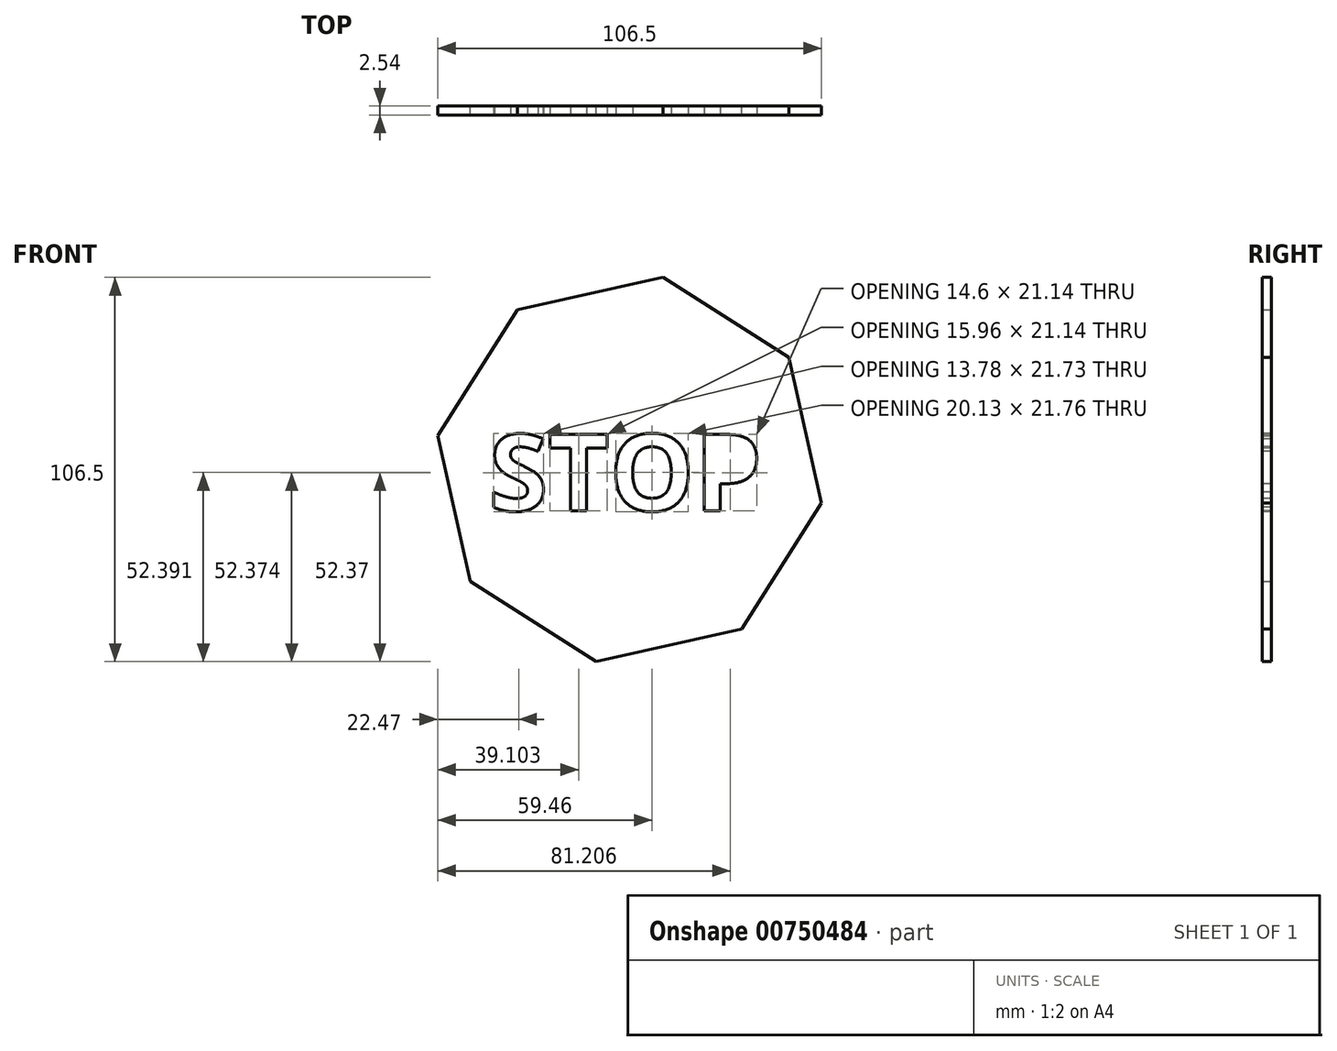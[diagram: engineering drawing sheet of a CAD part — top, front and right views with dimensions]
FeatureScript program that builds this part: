
annotation { "Feature Type Name" : "Feature", "Feature Type Description" : "" }
export const myFeature = defineFeature(function(context is Context, id is Id, definition is map)
    precondition{}
    {
        {
            var Q0;
            Q0=qCreatedBy(makeId("Front.planeOp"),FACE);
            var sketch = newSketch(context, id + "F0", { "sketchPlane" : qUnion([Q0])});
            skLineSegment(sketch, "E0.0", {"start": v(53.25, -9.32) * mm, "end": v(31.06, -44.25) * mm});
            skLineSegment(sketch, "E0.1", {"start": v(31.06, -44.25) * mm, "end": v(-9.32, -53.25) * mm});
            skLineSegment(sketch, "E0.2", {"start": v(-9.32, -53.25) * mm, "end": v(-44.25, -31.06) * mm});
            skLineSegment(sketch, "E0.3", {"start": v(-44.25, -31.06) * mm, "end": v(-53.25, 9.32) * mm});
            skLineSegment(sketch, "E0.4", {"start": v(-53.25, 9.32) * mm, "end": v(-31.06, 44.25) * mm});
            skLineSegment(sketch, "E0.5", {"start": v(-31.06, 44.25) * mm, "end": v(9.32, 53.25) * mm});
            skLineSegment(sketch, "E0.6", {"start": v(9.32, 53.25) * mm, "end": v(44.25, 31.06) * mm});
            skLineSegment(sketch, "E0.7", {"start": v(44.25, 31.06) * mm, "end": v(53.25, -9.32) * mm});
            skPoint(sketch, "E0.0.midPoint", {"position": v(42.16, -26.79) * mm});
            skPoint(sketch, "E1.0.midPoint", {"position": v(42.02, -21.88) * mm});
            skPoint(sketch, "E2.0.midPoint", {"position": v(27.79, -29.94) * mm});
            skPoint(sketch, "E3.orphan", {"position": v(26.24, 34.65) * mm});
            skPoint(sketch, "E4.orphan", {"position": v(-2.18, 43.41) * mm});
            skPoint(sketch, "E5.orphan", {"position": v(16.9, -40.05) * mm});
            skPoint(sketch, "E6.orphan", {"position": v(38.68, -19.82) * mm});
            skPoint(sketch, "E1.0.start.orphan", {"position": v(51.08, -4.48) * mm});
            skPoint(sketch, "E7.trimOffspring.end.orphan", {"position": v(32.95, -39.29) * mm});
            skLineSegment(sketch, "E8.trimOffspring", {"start": v(-49.94, 0.86) * mm, "end": v(-51.08, 4.48) * mm});
            skArc(sketch, "E9.trimOffspring", {"start": v(-0.86, -49.94) * mm, "mid": v(5.04, -49.7) * mm, "end": v(10.87, -48.75) * mm, "construction": true});
            skArc(sketch, "E10.trimOffspring", {"start": v(-49.94, 0.86) * mm, "mid": v(-49.7, -5.04) * mm, "end": v(-48.75, -10.87) * mm, "construction": true});
            skArc(sketch, "E11.trimOffspring", {"start": v(-34.7, 35.92) * mm, "mid": v(-38.7, 31.57) * mm, "end": v(-42.16, 26.79) * mm, "construction": true});
            skSolve(sketch);
        }
        {
            var Q0;
            Q0=makeQuery(id+"F0.imprint","IMPRINT",FACE,{"disambiguationData":[TD([[makeQuery(id+"F0.imprint","IMPRINT",EDGE,{"derivedFrom":sQuery(id+"F0.wireOp",EDGE,"E0.0")}),-1.0]])]});
            var Q1;
            Q1=makeQuery(id+"F0.imprint","IMPRINT",FACE,{"disambiguationData":[TD([[makeQuery(id+"F0.imprint","IMPRINT",EDGE,{"derivedFrom":sQuery(id+"F0.wireOp",EDGE,"E2.0")}),-1.0]])]});
            var Q2;
            Q2=makeQuery(id+"F0.imprint","IMPRINT",FACE,{"disambiguationData":[TD([[makeQuery(id+"F0.imprint","IMPRINT",EDGE,{"derivedFrom":sQuery(id+"F0.wireOp",EDGE,"E1.0")}),-1.0]])]});
            extrude(context, id + "F1", {"entities" : qUnion([Q0, Q1, Q2]), "depth" : 2.54 * mm, "offsetDistance" : 25.4 * mm});
        }
        {
            var Q0;
            Q0=qCreatedBy(makeId("Front.planeOp"),FACE);
            var sketch = newSketch(context, id + "F2", { "sketchPlane" : qUnion([Q0])});
            skPoint(sketch, "E12.0.midPoint", {"position": v(25, -5.92) * mm});
            skPoint(sketch, "E13.orphan", {"position": v(14.87, 21.73) * mm});
            skPoint(sketch, "E12.7.end.orphan", {"position": v(26.88, 4.44) * mm});
            skPoint(sketch, "E14.orphan", {"position": v(23.13, -16.28) * mm});
            skPoint(sketch, "E15.orphan", {"position": v(5.84, -28.28) * mm});
            skPoint(sketch, "E16.orphan", {"position": v(-14.87, -24.54) * mm});
            skPoint(sketch, "E17.orphan", {"position": v(-26.88, -7.25) * mm});
            skPoint(sketch, "E18.orphan", {"position": v(-23.13, 13.47) * mm});
            skText(sketch, "E19", { "text": "STOP", "fontName": "OpenSans-Bold.ttf"});
            const initialGuessF2  = {"E19": [-0.03903, -0.01145, 1, 0, 0.02132]};
            skSetInitialGuess(sketch, initialGuessF2);
            skSolve(sketch);
        }
        {
            var Q0;
            Q0 = qSketchRegion(id + "F2", true);
            extrude(context, id + "F3", {"entities" : qUnion([Q0]), "operationType" : NewBodyOperationType.ADD, "depth" : 2.8 * mm, "offsetDistance" : 25.4 * mm});
        }
        {
            var Q0;
            Q0=makeQuery(id+"F3.opExtrude","CAP_FACE",FACE,{"disambiguationData":[OSD([sQuery(id+"F2.wireOp",EDGE,"E19.sketch_text.stroke-28"),sQuery(id+"F2.wireOp",EDGE,"E19.sketch_text.stroke-29"),sQuery(id+"F2.wireOp",EDGE,"E19.sketch_text.stroke-30"),sQuery(id+"F2.wireOp",EDGE,"E19.sketch_text.stroke-31"),sQuery(id+"F2.wireOp",EDGE,"E19.sketch_text.stroke-32"),sQuery(id+"F2.wireOp",EDGE,"E19.sketch_text.stroke-33"),sQuery(id+"F2.wireOp",EDGE,"E19.sketch_text.stroke-34"),sQuery(id+"F2.wireOp",EDGE,"E19.sketch_text.stroke-35")])],"isStart":false});
            extrude(context, id + "F4", {"entities" : qUnion([Q0]), "operationType" : NewBodyOperationType.REMOVE, "oppositeDirection" : true, "depth" : 25.4 * mm, "offsetDistance" : 25.4 * mm});
        }
        {
            var Q0;
            Q0=makeQuery(id+"F3.opExtrude","CAP_FACE",FACE,{"disambiguationData":[OSD([sQuery(id+"F2.wireOp",EDGE,"E19.sketch_text.stroke-0"),sQuery(id+"F2.wireOp",EDGE,"E19.sketch_text.stroke-1"),sQuery(id+"F2.wireOp",EDGE,"E19.sketch_text.stroke-2"),sQuery(id+"F2.wireOp",EDGE,"E19.sketch_text.stroke-3"),sQuery(id+"F2.wireOp",EDGE,"E19.sketch_text.stroke-4"),sQuery(id+"F2.wireOp",EDGE,"E19.sketch_text.stroke-5"),sQuery(id+"F2.wireOp",EDGE,"E19.sketch_text.stroke-6"),sQuery(id+"F2.wireOp",EDGE,"E19.sketch_text.stroke-7"),sQuery(id+"F2.wireOp",EDGE,"E19.sketch_text.stroke-8"),sQuery(id+"F2.wireOp",EDGE,"E19.sketch_text.stroke-9"),sQuery(id+"F2.wireOp",EDGE,"E19.sketch_text.stroke-10"),sQuery(id+"F2.wireOp",EDGE,"E19.sketch_text.stroke-11"),sQuery(id+"F2.wireOp",EDGE,"E19.sketch_text.stroke-12"),sQuery(id+"F2.wireOp",EDGE,"E19.sketch_text.stroke-13"),sQuery(id+"F2.wireOp",EDGE,"E19.sketch_text.stroke-14"),sQuery(id+"F2.wireOp",EDGE,"E19.sketch_text.stroke-15"),sQuery(id+"F2.wireOp",EDGE,"E19.sketch_text.stroke-16"),sQuery(id+"F2.wireOp",EDGE,"E19.sketch_text.stroke-17"),sQuery(id+"F2.wireOp",EDGE,"E19.sketch_text.stroke-18"),sQuery(id+"F2.wireOp",EDGE,"E19.sketch_text.stroke-19"),sQuery(id+"F2.wireOp",EDGE,"E19.sketch_text.stroke-20"),sQuery(id+"F2.wireOp",EDGE,"E19.sketch_text.stroke-21"),sQuery(id+"F2.wireOp",EDGE,"E19.sketch_text.stroke-22"),sQuery(id+"F2.wireOp",EDGE,"E19.sketch_text.stroke-23"),sQuery(id+"F2.wireOp",EDGE,"E19.sketch_text.stroke-24"),sQuery(id+"F2.wireOp",EDGE,"E19.sketch_text.stroke-25"),sQuery(id+"F2.wireOp",EDGE,"E19.sketch_text.stroke-26"),sQuery(id+"F2.wireOp",EDGE,"E19.sketch_text.stroke-27")])],"isStart":false});
            extrude(context, id + "F5", {"entities" : qUnion([Q0]), "operationType" : NewBodyOperationType.REMOVE, "oppositeDirection" : true, "depth" : 25.4 * mm, "offsetDistance" : 25.4 * mm});
        }
        {
            var Q0;
            Q0=makeQuery(id+"F3.boolean.opBoolean","SPLIT",FACE,{"disambiguationData":[TD([makeQuery(id+"F3.opExtrude","SWEPT_FACE",FACE,{"disambiguationData":[OSD([sQuery(id+"F2.wireOp",EDGE,"E19.sketch_text.stroke-50")])]})])],"derivedFrom":makeQuery(id+"F1.opExtrude","CAP_FACE",FACE,{"disambiguationData":[OSD([sQuery(id+"F0.wireOp",EDGE,"E0.0"),sQuery(id+"F0.wireOp",EDGE,"E0.1"),sQuery(id+"F0.wireOp",EDGE,"E0.2"),sQuery(id+"F0.wireOp",EDGE,"E0.3"),sQuery(id+"F0.wireOp",EDGE,"E0.4"),sQuery(id+"F0.wireOp",EDGE,"E0.5"),sQuery(id+"F0.wireOp",EDGE,"E0.6"),sQuery(id+"F0.wireOp",EDGE,"E0.7")])],"isStart":false})});
            var Q1;
            Q1=makeQuery(id+"F3.opExtrude","CAP_FACE",FACE,{"disambiguationData":[OSD([sQuery(id+"F2.wireOp",EDGE,"E19.sketch_text.stroke-36"),sQuery(id+"F2.wireOp",EDGE,"E19.sketch_text.stroke-37"),sQuery(id+"F2.wireOp",EDGE,"E19.sketch_text.stroke-38"),sQuery(id+"F2.wireOp",EDGE,"E19.sketch_text.stroke-39"),sQuery(id+"F2.wireOp",EDGE,"E19.sketch_text.stroke-40"),sQuery(id+"F2.wireOp",EDGE,"E19.sketch_text.stroke-41"),sQuery(id+"F2.wireOp",EDGE,"E19.sketch_text.stroke-42"),sQuery(id+"F2.wireOp",EDGE,"E19.sketch_text.stroke-43"),sQuery(id+"F2.wireOp",EDGE,"E19.sketch_text.stroke-44"),sQuery(id+"F2.wireOp",EDGE,"E19.sketch_text.stroke-45"),sQuery(id+"F2.wireOp",EDGE,"E19.sketch_text.stroke-46"),sQuery(id+"F2.wireOp",EDGE,"E19.sketch_text.stroke-47"),sQuery(id+"F2.wireOp",EDGE,"E19.sketch_text.stroke-48"),sQuery(id+"F2.wireOp",EDGE,"E19.sketch_text.stroke-49")])],"isStart":false});
            var Q2;
            Q2=makeQuery(id+"F3.opExtrude","CAP_FACE",FACE,{"disambiguationData":[OSD([sQuery(id+"F2.wireOp",EDGE,"E19.sketch_text.stroke-50"),sQuery(id+"F2.wireOp",EDGE,"E19.sketch_text.stroke-51"),sQuery(id+"F2.wireOp",EDGE,"E19.sketch_text.stroke-52"),sQuery(id+"F2.wireOp",EDGE,"E19.sketch_text.stroke-53"),sQuery(id+"F2.wireOp",EDGE,"E19.sketch_text.stroke-54"),sQuery(id+"F2.wireOp",EDGE,"E19.sketch_text.stroke-55"),sQuery(id+"F2.wireOp",EDGE,"E19.sketch_text.stroke-56"),sQuery(id+"F2.wireOp",EDGE,"E19.sketch_text.stroke-57"),sQuery(id+"F2.wireOp",EDGE,"E19.sketch_text.stroke-58"),sQuery(id+"F2.wireOp",EDGE,"E19.sketch_text.stroke-59"),sQuery(id+"F2.wireOp",EDGE,"E19.sketch_text.stroke-60"),sQuery(id+"F2.wireOp",EDGE,"E19.sketch_text.stroke-61"),sQuery(id+"F2.wireOp",EDGE,"E19.sketch_text.stroke-62"),sQuery(id+"F2.wireOp",EDGE,"E19.sketch_text.stroke-63"),sQuery(id+"F2.wireOp",EDGE,"E19.sketch_text.stroke-64"),sQuery(id+"F2.wireOp",EDGE,"E19.sketch_text.stroke-65")])],"isStart":false});
            extrude(context, id + "F6", {"entities" : qUnion([Q0, Q1, Q2]), "operationType" : NewBodyOperationType.REMOVE, "oppositeDirection" : true, "depth" : 25.4 * mm, "offsetDistance" : 25.4 * mm});
        }
    });
